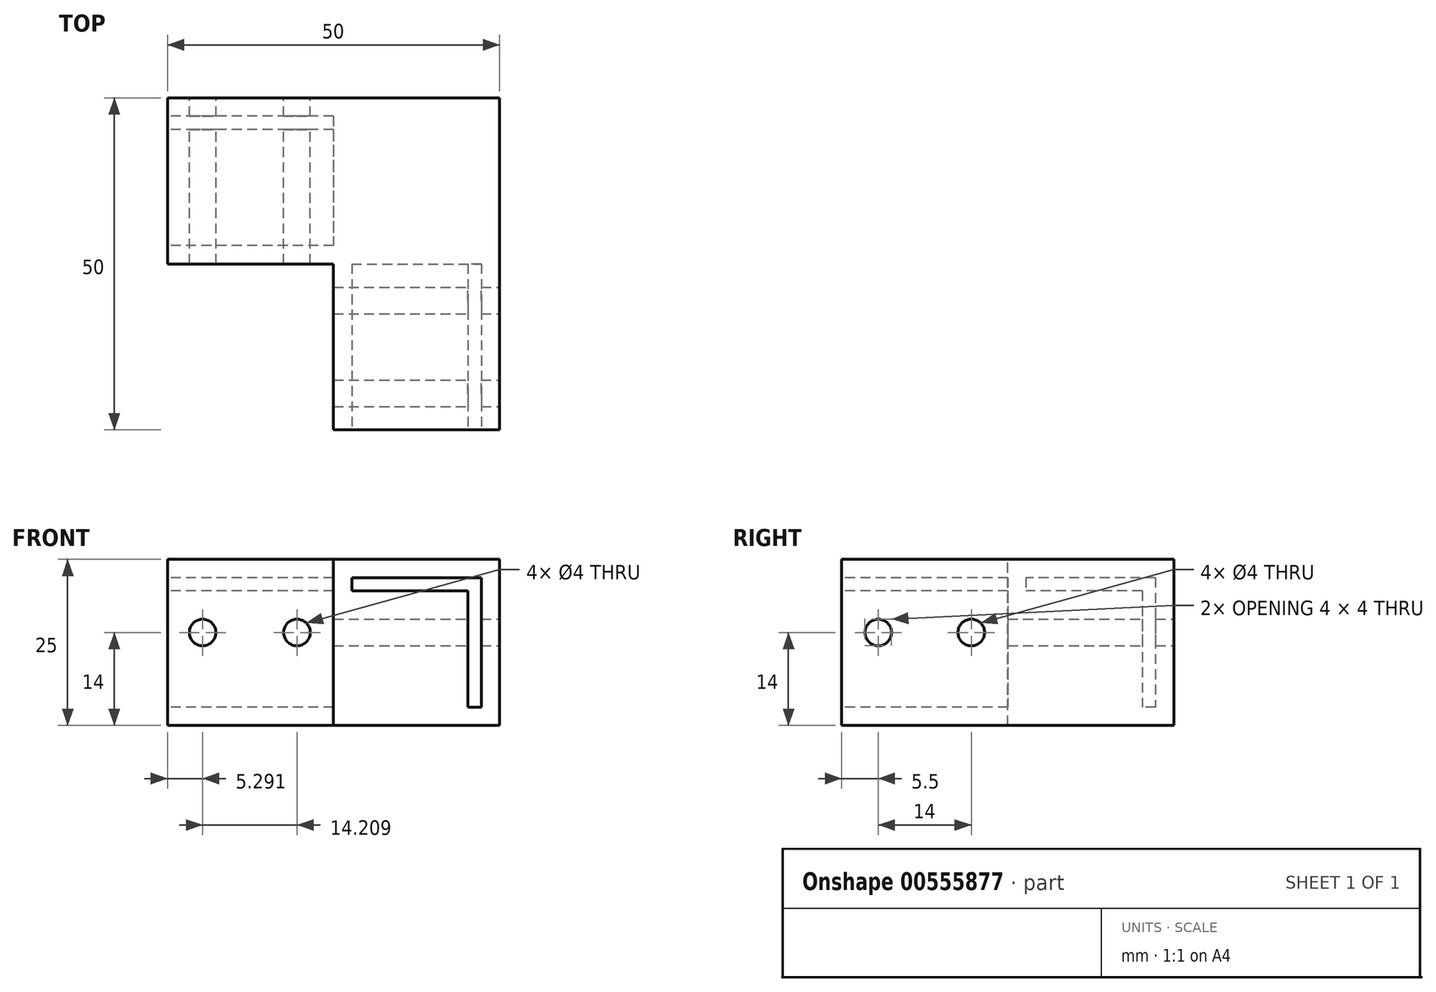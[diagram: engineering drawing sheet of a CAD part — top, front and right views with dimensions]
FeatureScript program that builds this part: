
annotation { "Feature Type Name" : "Feature", "Feature Type Description" : "" }
export const myFeature = defineFeature(function(context is Context, id is Id, definition is map)
    precondition{}
    {
        {
            var Q0;
            Q0=qCreatedBy(makeId("Top.planeOp"),FACE);
            var sketch = newSketch(context, id + "F0", { "sketchPlane" : qUnion([Q0])});
            skLineSegment(sketch, "E0.bottom", {"start": v(0, 0) * mm, "end": v(25, 0) * mm});
            skLineSegment(sketch, "E0.top", {"start": v(0, 25) * mm, "end": v(25, 25) * mm});
            skLineSegment(sketch, "E0.left", {"start": v(0, 0) * mm, "end": v(0, 25) * mm});
            skLineSegment(sketch, "E0.right", {"start": v(25, 0) * mm, "end": v(25, 25) * mm});
            skSolve(sketch);
        }
        {
            var Q0;
            Q0=makeQuery(id+"F0.imprint","IMPRINT",FACE,{"disambiguationData":[TD([[makeQuery(id+"F0.imprint","IMPRINT",EDGE,{"derivedFrom":sQuery(id+"F0.wireOp",EDGE,"E0.bottom")}),1.0]])]});
            extrude(context, id + "F1", {"entities" : qUnion([Q0]), "depth" : 25 * mm, "offsetDistance" : 25 * mm});
        }
        {
            var Q0;
            Q0=makeQuery(id+"F1.opExtrude","SWEPT_FACE",FACE,{"disambiguationData":[OSD([sQuery(id+"F0.wireOp",EDGE,"E0.bottom")])]});
            extrude(context, id + "F2", {"entities" : qUnion([Q0]), "operationType" : NewBodyOperationType.ADD, "depth" : 25 * mm, "offsetDistance" : 25 * mm});
        }
        {
            var Q0;
            {var subQ0=sQuery(id+"F0.wireOp",EDGE,"E0.left");Q0=makeQuery(id+"F2.boolean.opBoolean","MERGE",FACE,{"derivedFrom":[makeQuery(id+"F1.opExtrude","SWEPT_FACE",FACE,{"disambiguationData":[OSD([subQ0])]}),makeQuery(id+"F2.opExtrude","SWEPT_FACE",FACE,{"disambiguationData":[OSD([sQuery(id+"F0.wireOp",EDGE,"E0.bottom"),subQ0])]})]});}
            var Q1;
            Q1 = qSketchRegion(id + "F4", true);
            extrude(context, id + "F3", {"entities" : qUnion([Q0, Q1]), "operationType" : NewBodyOperationType.ADD, "depth" : 25 * mm, "offsetDistance" : 25 * mm});
        }
        {
            var Q0;
            {var subQ0=sQuery(id+"F0.wireOp",EDGE,"E0.left");var subQ1=sQuery(id+"F0.wireOp",EDGE,"E0.bottom");Q0=makeQuery(id+"F3.boolean.opBoolean","MERGE",FACE,{"derivedFrom":[makeQuery(id+"F2.boolean.opBoolean","MERGE",FACE,{"derivedFrom":[makeQuery(id+"F1.opExtrude","CAP_FACE",FACE,{"disambiguationData":[OSD([subQ1,sQuery(id+"F0.wireOp",EDGE,"E0.top"),subQ0,sQuery(id+"F0.wireOp",EDGE,"E0.right")])],"isStart":false}),makeQuery(id+"F2.opExtrude","SWEPT_FACE",FACE,{"disambiguationData":[OSD([subQ1]),TDD([makeQuery(id+"F1.opExtrude","CAP_EDGE",EDGE,{"disambiguationData":[OSD([subQ1])],"isStart":false})])]})]}),makeQuery(id+"F3.opExtrude","SWEPT_FACE",FACE,{"disambiguationData":[OSD([subQ1,subQ0]),TDD([makeQuery(id+"F2.boolean.opBoolean","MERGE",EDGE,{"derivedFrom":[makeQuery(id+"F1.opExtrude","CAP_EDGE",EDGE,{"disambiguationData":[OSD([subQ0])],"isStart":false}),makeQuery(id+"F2.opExtrude","SWEPT_EDGE",EDGE,{"disambiguationData":[OSD([subQ1,subQ0]),TDD([makeQuery(id+"F1.opExtrude","CAP_VERTEX",VERTEX,{"disambiguationData":[OSD([subQ1,subQ0])],"isStart":false})])]})]})])]})]});}
            var sketch = newSketch(context, id + "F4", { "sketchPlane" : qUnion([Q0])});
            skLineSegment(sketch, "E1.bottom", {"start": v(0, 0) * mm, "end": v(-25, 0) * mm});
            skLineSegment(sketch, "E1.top", {"start": v(0, -25) * mm, "end": v(-25, -25) * mm});
            skLineSegment(sketch, "E1.left", {"start": v(0, 0) * mm, "end": v(0, -25) * mm});
            skLineSegment(sketch, "E1.right", {"start": v(-25, 0) * mm, "end": v(-25, -25) * mm});
            skSolve(sketch);
        }
        {
            var Q0;
            Q0=makeQuery(id+"F4.imprint","IMPRINT",FACE,{"disambiguationData":[TD([[makeQuery(id+"F4.imprint","IMPRINT",EDGE,{"derivedFrom":sQuery(id+"F4.wireOp",EDGE,"E1.bottom")}),1.0]])]});
            extrude(context, id + "F5", {"entities" : qUnion([Q0]), "operationType" : NewBodyOperationType.REMOVE, "oppositeDirection" : true, "depth" : 25 * mm, "offsetDistance" : 25 * mm});
        }
        {
            var Q0;
            {var subQ0=sQuery(id+"F0.wireOp",EDGE,"E0.left");var subQ1=sQuery(id+"F0.wireOp",EDGE,"E0.bottom");Q0=makeQuery(id+"F3.boolean.opBoolean","MERGE",FACE,{"derivedFrom":[makeQuery(id+"F2.opExtrude","CAP_FACE",FACE,{"disambiguationData":[OSD([subQ1])],"isStart":false}),makeQuery(id+"F3.opExtrude","SWEPT_FACE",FACE,{"disambiguationData":[OSD([subQ1,subQ0]),TDD([makeQuery(id+"F2.opExtrude","CAP_EDGE",EDGE,{"disambiguationData":[OSD([subQ1,subQ0])],"isStart":false})])]})]});}
            var sketch = newSketch(context, id + "F6", { "sketchPlane" : qUnion([Q0])});
            skLineSegment(sketch, "E2.bottom", {"start": v(2.75, 22.25) * mm, "end": v(22.25, 22.25) * mm});
            skLineSegment(sketch, "E2.top", {"start": v(2.75, 20.25) * mm, "end": v(22.25, 20.25) * mm});
            skLineSegment(sketch, "E2.left", {"start": v(2.75, 22.25) * mm, "end": v(2.75, 20.25) * mm});
            skLineSegment(sketch, "E2.right", {"start": v(22.25, 22.25) * mm, "end": v(22.25, 20.25) * mm});
            skLineSegment(sketch, "E3.bottom", {"start": v(22.25, 22.25) * mm, "end": v(20.25, 22.25) * mm});
            skLineSegment(sketch, "E3.top", {"start": v(22.25, 2.75) * mm, "end": v(20.25, 2.75) * mm});
            skLineSegment(sketch, "E3.left", {"start": v(22.25, 22.25) * mm, "end": v(22.25, 2.75) * mm});
            skLineSegment(sketch, "E3.right", {"start": v(20.25, 22.25) * mm, "end": v(20.25, 2.75) * mm});
            skSolve(sketch);
        }
        {
            var Q0;
            Q0 = qSketchRegion(id + "F6", true);
            extrude(context, id + "F7", {"entities" : qUnion([Q0]), "operationType" : NewBodyOperationType.REMOVE, "oppositeDirection" : true, "depth" : 25 * mm, "offsetDistance" : 25 * mm});
        }
        {
            var Q0;
            Q0=makeQuery(id+"F3.opExtrude","CAP_FACE",FACE,{"disambiguationData":[OSD([sQuery(id+"F0.wireOp",EDGE,"E0.bottom"),sQuery(id+"F0.wireOp",EDGE,"E0.left")])],"isStart":false});
            var sketch = newSketch(context, id + "F8", { "sketchPlane" : qUnion([Q0])});
            skLineSegment(sketch, "E4.bottom", {"start": v(-22.25, 22.25) * mm, "end": v(-2.75, 22.25) * mm});
            skLineSegment(sketch, "E4.top", {"start": v(-22.25, 20.25) * mm, "end": v(-2.75, 20.25) * mm});
            skLineSegment(sketch, "E4.left", {"start": v(-22.25, 22.25) * mm, "end": v(-22.25, 20.25) * mm});
            skLineSegment(sketch, "E4.right", {"start": v(-2.75, 22.25) * mm, "end": v(-2.75, 20.25) * mm});
            skLineSegment(sketch, "E5.bottom", {"start": v(-22.25, 22.25) * mm, "end": v(-20.25, 22.25) * mm});
            skLineSegment(sketch, "E5.top", {"start": v(-22.25, 2.75) * mm, "end": v(-20.25, 2.75) * mm});
            skLineSegment(sketch, "E5.left", {"start": v(-22.25, 22.25) * mm, "end": v(-22.25, 2.75) * mm});
            skLineSegment(sketch, "E5.right", {"start": v(-20.25, 22.25) * mm, "end": v(-20.25, 2.75) * mm});
            skSolve(sketch);
        }
        {
            var Q0;
            Q0 = qSketchRegion(id + "F8", true);
            extrude(context, id + "F9", {"entities" : qUnion([Q0]), "operationType" : NewBodyOperationType.REMOVE, "oppositeDirection" : true, "depth" : 25 * mm, "offsetDistance" : 25 * mm});
        }
        {
            var Q0;
            {var subQ0=sQuery(id+"F0.wireOp",EDGE,"E0.top");Q0=makeQuery(id+"F3.boolean.opBoolean","MERGE",FACE,{"derivedFrom":[makeQuery(id+"F1.opExtrude","SWEPT_FACE",FACE,{"disambiguationData":[OSD([subQ0])]}),makeQuery(id+"F3.opExtrude","SWEPT_FACE",FACE,{"disambiguationData":[OSD([subQ0,sQuery(id+"F0.wireOp",EDGE,"E0.left")])]})]});}
            var sketch = newSketch(context, id + "F10", { "sketchPlane" : qUnion([Q0])});
            skCircle(sketch, "E6", {"center": v(19.7, 14) * mm, "radius": 2 * mm});
            skCircle(sketch, "E7", {"center": v(5.5, 14) * mm, "radius": 2 * mm});
            skSolve(sketch);
        }
        {
            var Q0;
            Q0 = qSketchRegion(id + "F10", true);
            extrude(context, id + "F11", {"entities" : qUnion([Q0]), "operationType" : NewBodyOperationType.REMOVE, "oppositeDirection" : true, "depth" : 25 * mm, "offsetDistance" : 25 * mm});
        }
        {
            var Q0;
            {var subQ0=sQuery(id+"F0.wireOp",EDGE,"E0.right");Q0=makeQuery(id+"F2.boolean.opBoolean","MERGE",FACE,{"derivedFrom":[makeQuery(id+"F1.opExtrude","SWEPT_FACE",FACE,{"disambiguationData":[OSD([subQ0])]}),makeQuery(id+"F2.opExtrude","SWEPT_FACE",FACE,{"disambiguationData":[OSD([sQuery(id+"F0.wireOp",EDGE,"E0.bottom"),subQ0])]})]});}
            var sketch = newSketch(context, id + "F12", { "sketchPlane" : qUnion([Q0])});
            skCircle(sketch, "E8", {"center": v(-19.5, 14) * mm, "radius": 2 * mm});
            skCircle(sketch, "E9", {"center": v(-5.5, 14) * mm, "radius": 2 * mm});
            skSolve(sketch);
        }
        {
            var Q0;
            Q0 = qSketchRegion(id + "F12", true);
            extrude(context, id + "F13", {"entities" : qUnion([Q0]), "operationType" : NewBodyOperationType.REMOVE, "oppositeDirection" : true, "depth" : 25 * mm, "offsetDistance" : 25 * mm});
        }
    });
